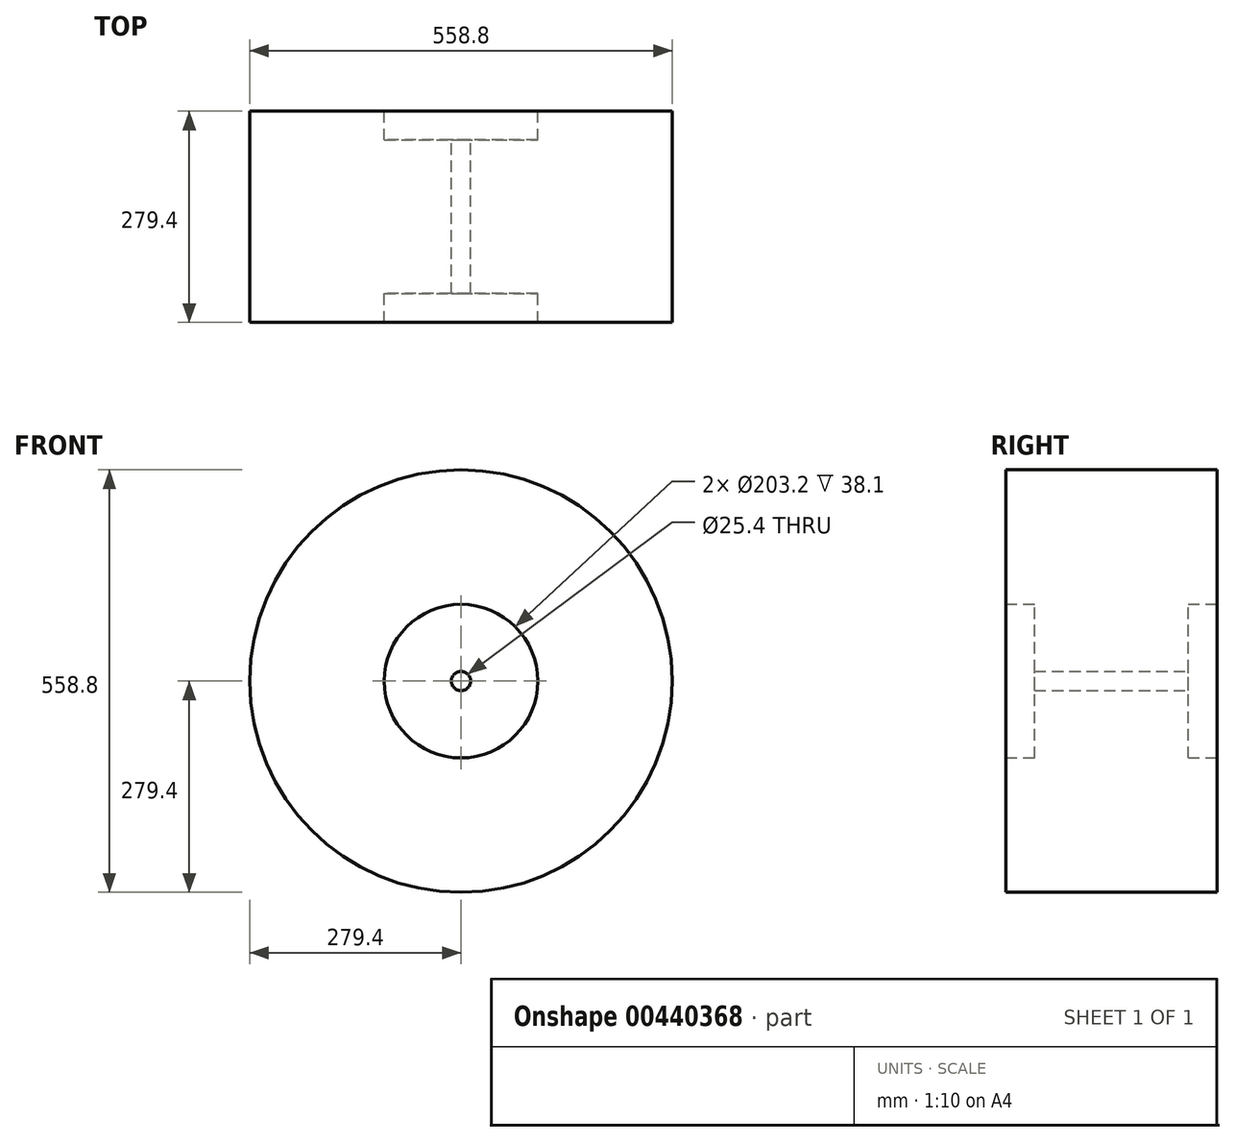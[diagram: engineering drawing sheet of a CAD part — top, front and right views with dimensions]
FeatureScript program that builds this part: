
annotation { "Feature Type Name" : "Feature", "Feature Type Description" : "" }
export const myFeature = defineFeature(function(context is Context, id is Id, definition is map)
    precondition{}
    {
        {
            var Q0;
            Q0=qCreatedBy(makeId("Front.planeOp"),FACE);
            var sketch = newSketch(context, id + "F0", { "sketchPlane" : qUnion([Q0])});
            skCircle(sketch, "E0", {"center": v(0, 0) * mm, "radius": 279.4 * mm});
            skCircle(sketch, "E1", {"center": v(0, 0) * mm, "radius": 101.6 * mm});
            skSolve(sketch);
        }
        {
            var Q0;
            Q0=makeQuery(id+"F0.imprint","IMPRINT",FACE,{"disambiguationData":[TD([[makeQuery(id+"F0.imprint","IMPRINT",EDGE,{"derivedFrom":sQuery(id+"F0.wireOp",EDGE,"E0")}),1.0]])]});
            var sketch = newSketch(context, id + "F1", { "sketchPlane" : qUnion([Q0])});
            skCircle(sketch, "E2", {"center": v(0, 0) * mm, "radius": 12.7 * mm});
            skSolve(sketch);
        }
        {
            var Q0;
            Q0=makeQuery(id+"F0.imprint","IMPRINT",FACE,{"disambiguationData":[TD([[makeQuery(id+"F0.imprint","IMPRINT",EDGE,{"derivedFrom":sQuery(id+"F0.wireOp",EDGE,"E0")}),1.0]])]});
            extrude(context, id + "F2", {"entities" : qUnion([Q0]), "endBound" : BoundingType.SYMMETRIC, "depth" : 279.4 * mm});
        }
        {
            var Q0;
            Q0=makeQuery(id+"F1.imprint","IMPRINT",FACE,{"disambiguationData":[TD([[makeQuery(id+"F1.imprint","IMPRINT",EDGE,{"derivedFrom":sQuery(id+"F1.wireOp",EDGE,"E2")}),-1.0]])]});
            extrude(context, id + "F3", {"entities" : qUnion([Q0]), "operationType" : NewBodyOperationType.ADD, "endBound" : BoundingType.SYMMETRIC, "depth" : 203.2 * mm});
        }
    });
